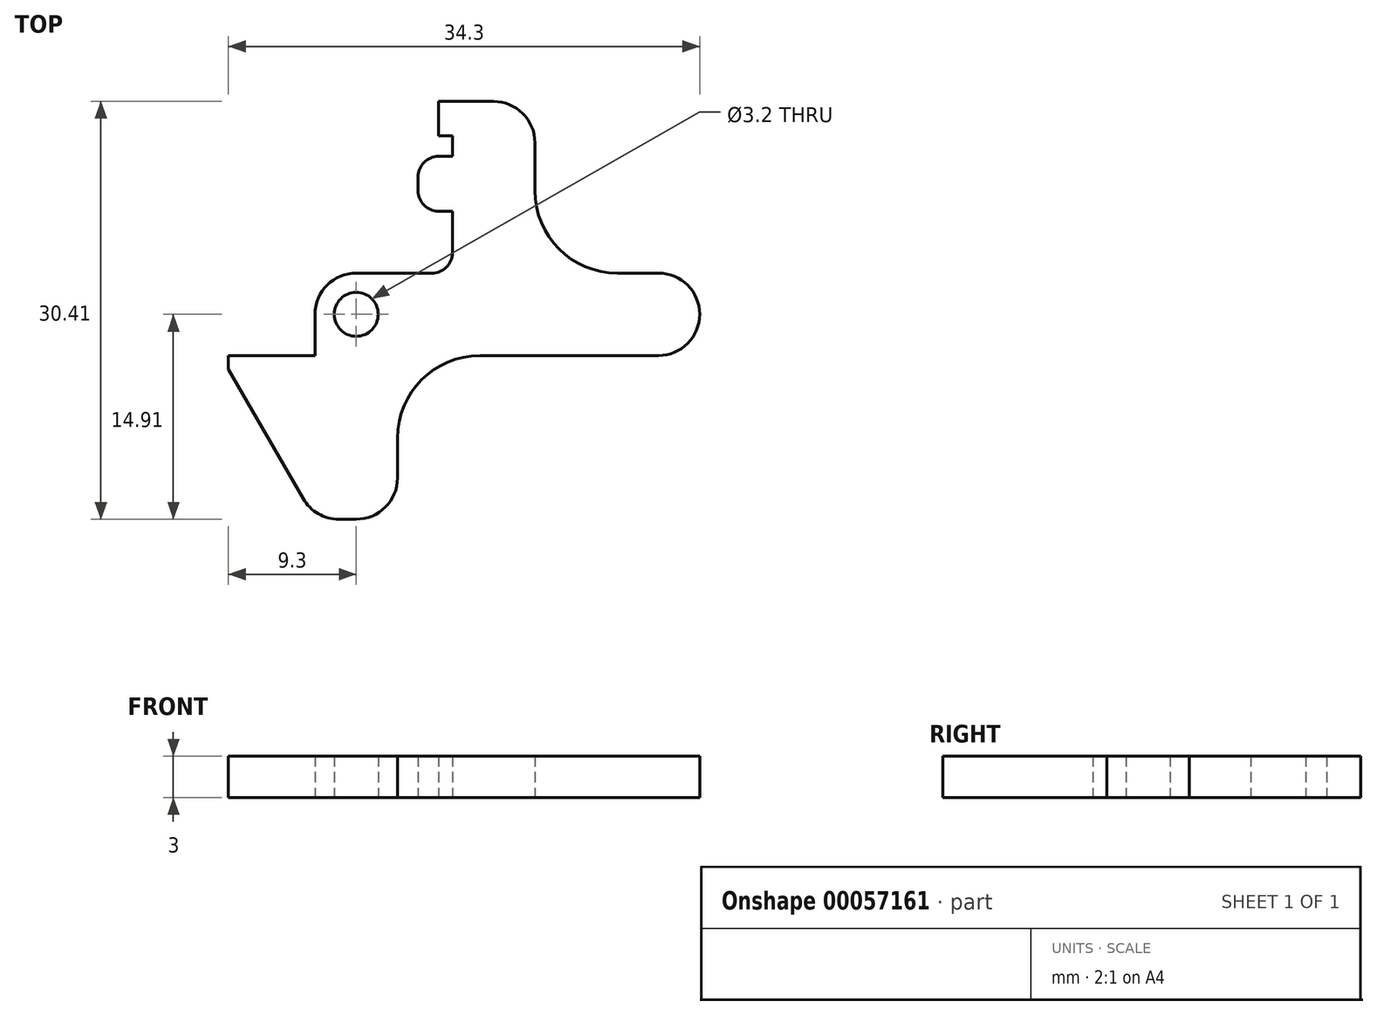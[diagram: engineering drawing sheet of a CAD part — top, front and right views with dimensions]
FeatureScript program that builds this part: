
annotation { "Feature Type Name" : "Feature", "Feature Type Description" : "" }
export const myFeature = defineFeature(function(context is Context, id is Id, definition is map)
    precondition{}
    {
        {
            var Q0;
            Q0=qCreatedBy(makeId("Top.planeOp"),FACE);
            var sketch = newSketch(context, id + "F0", { "sketchPlane" : qUnion([Q0])});
            skCircle(sketch, "E0", {"center": v(0, 0) * mm, "radius": 1.6 * mm});
            skCircle(sketch, "E1", {"center": v(0, 0) * mm, "radius": 3 * mm, "construction": true});
            skLineSegment(sketch, "E2", {"start": v(-3, 0) * mm, "end": v(-3, -4) * mm});
            skLineSegment(sketch, "E3", {"start": v(-3, -4) * mm, "end": v(-9.3, -4) * mm});
            skLineSegment(sketch, "E4", {"start": v(-9.3, -4) * mm, "end": v(-3, -14.91) * mm});
            skLineSegment(sketch, "E5", {"start": v(-3, -14.91) * mm, "end": v(3, -14.91) * mm});
            skLineSegment(sketch, "E6", {"start": v(0, 3) * mm, "end": v(25, 3) * mm});
            skArc(sketch, "E7", {"start": v(-3, 0) * mm, "mid": v(-2.12, 2.12) * mm, "end": v(0, 3) * mm});
            skLineSegment(sketch, "E8", {"start": v(-3, -4) * mm, "end": v(-3, -14.91) * mm, "construction": true});
            skLineSegment(sketch, "E9", {"start": v(3, -14.91) * mm, "end": v(3, -3) * mm});
            skLineSegment(sketch, "E10", {"start": v(25, 3) * mm, "end": v(25, -3) * mm});
            skLineSegment(sketch, "E11", {"start": v(25, -3) * mm, "end": v(3, -3) * mm});
            skLineSegment(sketch, "E12", {"start": v(7, 3) * mm, "end": v(7, 13) * mm});
            skLineSegment(sketch, "E13", {"start": v(7, 13) * mm, "end": v(13, 13) * mm});
            skLineSegment(sketch, "E14", {"start": v(13, 13) * mm, "end": v(13, 3) * mm});
            skLineSegment(sketch, "E15.bottom", {"start": v(7, 11.5) * mm, "end": v(4.5, 11.5) * mm});
            skLineSegment(sketch, "E15.top", {"start": v(7, 7.5) * mm, "end": v(4.5, 7.5) * mm});
            skLineSegment(sketch, "E15.left", {"start": v(7, 11.5) * mm, "end": v(7, 7.5) * mm});
            skLineSegment(sketch, "E15.right", {"start": v(4.5, 11.5) * mm, "end": v(4.5, 7.5) * mm});
            skLineSegment(sketch, "E16.bottom", {"start": v(13, 13) * mm, "end": v(6, 13) * mm});
            skLineSegment(sketch, "E16.top", {"start": v(13, 15.5) * mm, "end": v(6, 15.5) * mm});
            skLineSegment(sketch, "E16.left", {"start": v(13, 13) * mm, "end": v(13, 15.5) * mm});
            skLineSegment(sketch, "E16.right", {"start": v(6, 13) * mm, "end": v(6, 15.5) * mm});
            skLineSegment(sketch, "E17.bottom", {"start": v(-9.3, -4) * mm, "end": v(-3, -4) * mm});
            skLineSegment(sketch, "E17.top", {"start": v(-9.3, -3) * mm, "end": v(-3, -3) * mm});
            skLineSegment(sketch, "E17.left", {"start": v(-9.3, -4) * mm, "end": v(-9.3, -3) * mm});
            skLineSegment(sketch, "E17.right", {"start": v(-3, -4) * mm, "end": v(-3, -3) * mm});
            skSolve(sketch);
        }
        {
            var Q0;
            Q0 = qSketchRegion(id + "F0", true);
            extrude(context, id + "F1", {"entities" : qUnion([Q0]), "depth" : 3 * mm});
        }
        {
            var Q0;
            Q0=makeQuery(id+"F1.opExtrude","SWEPT_EDGE",EDGE,{"disambiguationData":[OSD([sQuery(id+"F0.wireOp",EDGE,"E4"),sQuery(id+"F0.wireOp",EDGE,"E5")])]});
            var Q1;
            Q1=makeQuery(id+"F1.opExtrude","SWEPT_EDGE",EDGE,{"disambiguationData":[OSD([sQuery(id+"F0.wireOp",EDGE,"E5"),sQuery(id+"F0.wireOp",EDGE,"E9")])]});
            var Q2;
            Q2=makeQuery(id+"F1.opExtrude","SWEPT_EDGE",EDGE,{"disambiguationData":[OSD([sQuery(id+"F0.wireOp",EDGE,"E10"),sQuery(id+"F0.wireOp",EDGE,"E11")])]});
            var Q3;
            Q3=makeQuery(id+"F1.opExtrude","SWEPT_EDGE",EDGE,{"disambiguationData":[OSD([sQuery(id+"F0.wireOp",EDGE,"E6"),sQuery(id+"F0.wireOp",EDGE,"E10")])]});
            var Q4;
            Q4=makeQuery(id+"F1.opExtrude","SWEPT_EDGE",EDGE,{"disambiguationData":[OSD([sQuery(id+"F0.wireOp",EDGE,"E16.top"),sQuery(id+"F0.wireOp",EDGE,"E16.left")])]});
            fillet(context, id + "F2", {"entities" : qUnion([Q0, Q1, Q2, Q3, Q4]), "radius" : 3 * mm, "allowEdgeOverflow" : false});
        }
        {
            var Q0;
            Q0=makeQuery(id+"F1.opExtrude","SWEPT_EDGE",EDGE,{"disambiguationData":[OSD([sQuery(id+"F0.wireOp",EDGE,"E9"),sQuery(id+"F0.wireOp",EDGE,"E11")])]});
            var Q1;
            Q1=makeQuery(id+"F1.opExtrude","SWEPT_EDGE",EDGE,{"disambiguationData":[OSD([sQuery(id+"F0.wireOp",EDGE,"E6"),sQuery(id+"F0.wireOp",EDGE,"E14")])]});
            fillet(context, id + "F3", {"entities" : qUnion([Q0, Q1]), "radius" : 6 * mm, "tangentPropagation" : true, "allowEdgeOverflow" : false});
        }
        {
            var Q0;
            Q0=makeQuery(id+"F1.opExtrude","SWEPT_EDGE",EDGE,{"disambiguationData":[OSD([sQuery(id+"F0.wireOp",EDGE,"E15.bottom"),sQuery(id+"F0.wireOp",EDGE,"E15.right")])]});
            var Q1;
            Q1=makeQuery(id+"F1.opExtrude","SWEPT_EDGE",EDGE,{"disambiguationData":[OSD([sQuery(id+"F0.wireOp",EDGE,"E15.top"),sQuery(id+"F0.wireOp",EDGE,"E15.right")])]});
            var Q2;
            Q2=makeQuery(id+"F1.opExtrude","SWEPT_EDGE",EDGE,{"disambiguationData":[OSD([sQuery(id+"F0.wireOp",EDGE,"E6"),sQuery(id+"F0.wireOp",EDGE,"E12")])]});
            fillet(context, id + "F4", {"entities" : qUnion([Q0, Q1, Q2]), "radius" : 1.5 * mm, "tangentPropagation" : true, "allowEdgeOverflow" : false});
        }
    });
